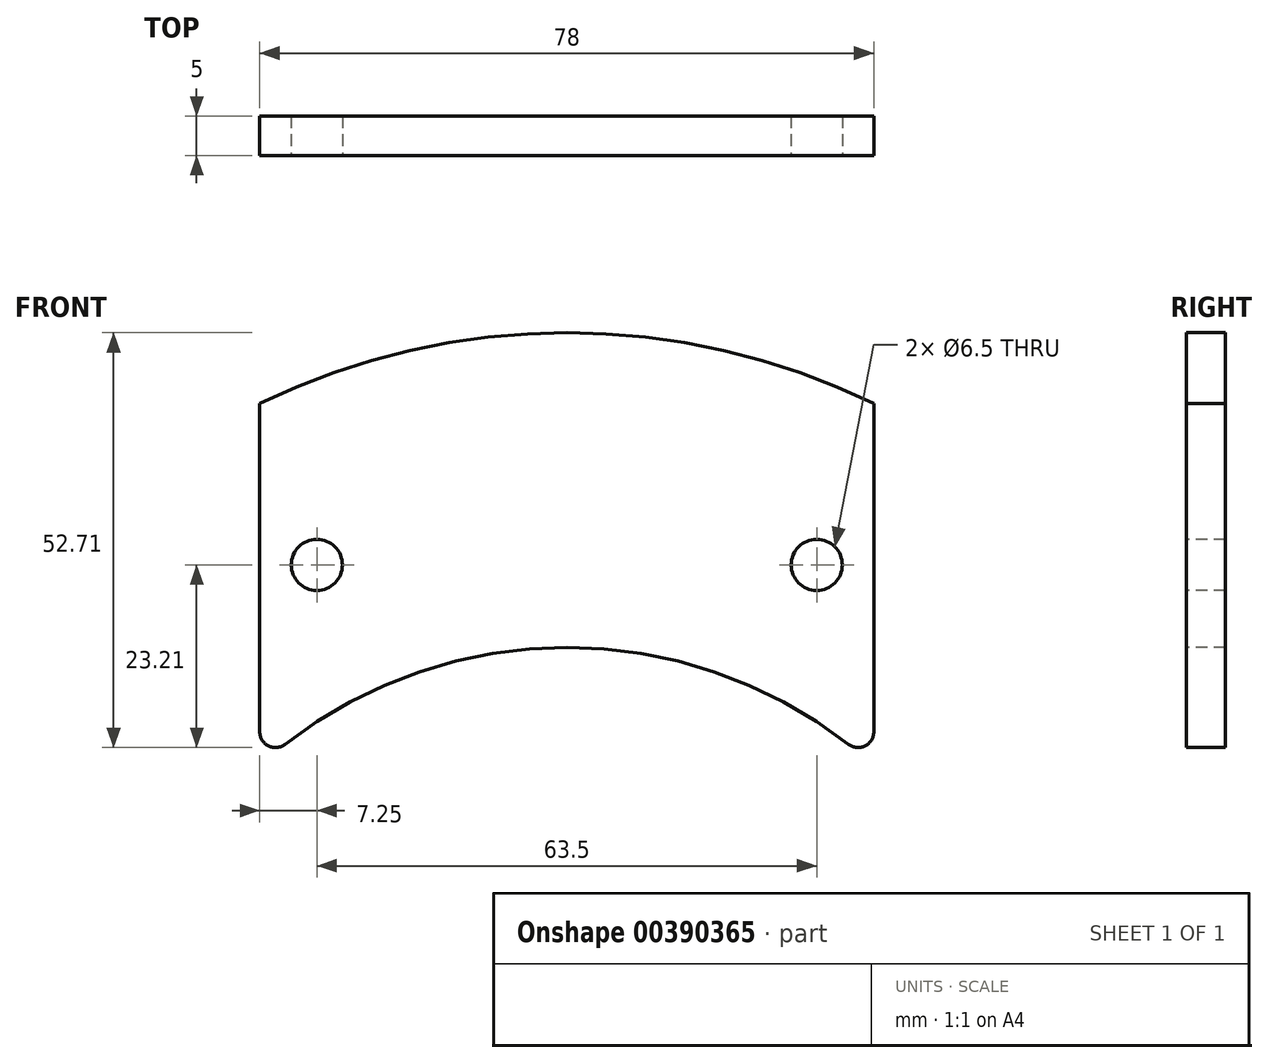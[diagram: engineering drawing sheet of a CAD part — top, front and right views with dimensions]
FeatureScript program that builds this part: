
annotation { "Feature Type Name" : "Feature", "Feature Type Description" : "" }
export const myFeature = defineFeature(function(context is Context, id is Id, definition is map)
    precondition{}
    {
        {
            var Q0;
            Q0=qCreatedBy(makeId("Front.planeOp"),FACE);
            var sketch = newSketch(context, id + "F0", { "sketchPlane" : qUnion([Q0])});
            skLineSegment(sketch, "E0", {"start": v(-39, -46) * mm, "end": v(-39, 0) * mm});
            skLineSegment(sketch, "E1", {"start": v(-39, 0) * mm, "end": v(39, 0) * mm, "construction": true});
            skLineSegment(sketch, "E2", {"start": v(39, 0) * mm, "end": v(39, -46) * mm});
            skArc(sketch, "E3", {"start": v(39, -46) * mm, "mid": v(0, -31) * mm, "end": v(-39, -46) * mm});
            skCircle(sketch, "E4", {"center": v(-31.75, -20.5) * mm, "radius": 3.25 * mm});
            skCircle(sketch, "E5", {"center": v(31.75, -20.5) * mm, "radius": 3.25 * mm});
            skArc(sketch, "E6", {"start": v(39, 0) * mm, "mid": v(0, 9) * mm, "end": v(-39, 0) * mm});
            skSolve(sketch);
        }
        {
            var Q0;
            Q0=qSketchRegion(id+"F0",true);
            extrude(context, id + "F1", {"entities" : qUnion([Q0]), "oppositeDirection" : true, "depth" : 5 * mm});
        }
        {
            var Q0;
            Q0=makeQuery(id+"F1.opExtrude","SWEPT_EDGE",EDGE,{"disambiguationData":[OSD([sQuery(id+"F0.wireOp",EDGE,"E0"),sQuery(id+"F0.wireOp",EDGE,"E3")])]});
            var Q1;
            Q1=makeQuery(id+"F1.opExtrude","SWEPT_EDGE",EDGE,{"disambiguationData":[OSD([sQuery(id+"F0.wireOp",EDGE,"E2"),sQuery(id+"F0.wireOp",EDGE,"E3")])]});
            fillet(context, id + "F2", {"entities" : qUnion([Q0, Q1]), "radius" : 2 * mm, "tangentPropagation" : true, "allowEdgeOverflow" : false});
        }
    });
